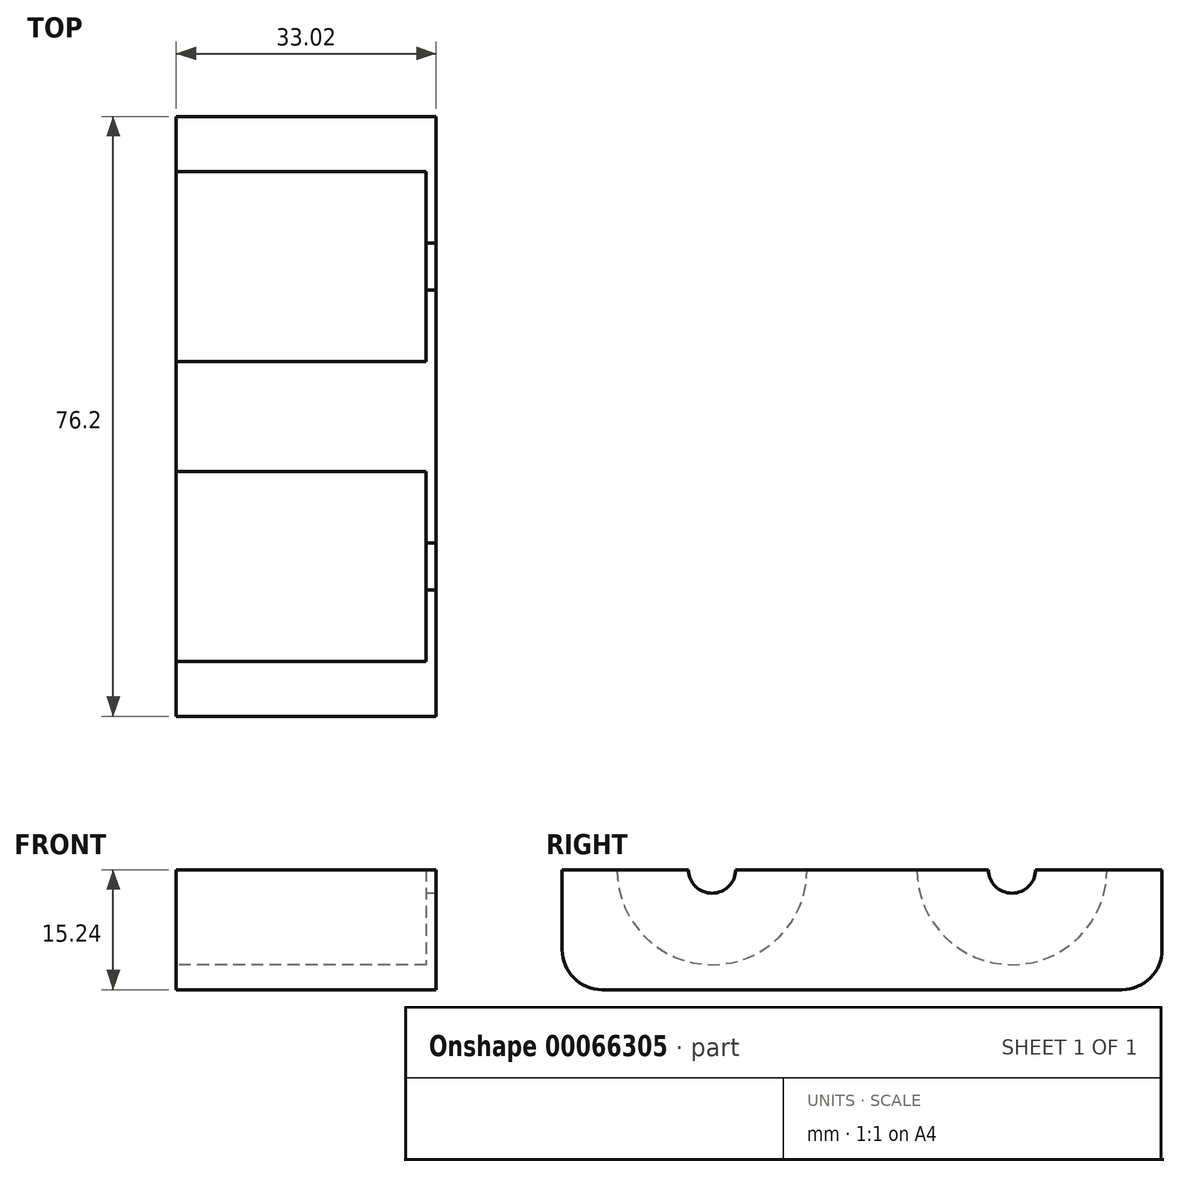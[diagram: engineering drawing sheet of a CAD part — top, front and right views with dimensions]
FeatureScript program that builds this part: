
annotation { "Feature Type Name" : "Feature", "Feature Type Description" : "" }
export const myFeature = defineFeature(function(context is Context, id is Id, definition is map)
    precondition{}
    {
        {
            var Q0;
            Q0=qCreatedBy(makeId("Right.planeOp"),FACE);
            var sketch = newSketch(context, id + "F0", { "sketchPlane" : qUnion([Q0])});
            skLineSegment(sketch, "E0.bottom", {"start": v(-38.1, 0) * mm, "end": v(38.1, 0) * mm});
            skLineSegment(sketch, "E0.top", {"start": v(-38.1, -15.24) * mm, "end": v(38.1, -15.24) * mm});
            skLineSegment(sketch, "E0.left", {"start": v(-38.1, 0) * mm, "end": v(-38.1, -15.24) * mm});
            skLineSegment(sketch, "E0.right", {"start": v(38.1, 0) * mm, "end": v(38.1, -15.24) * mm});
            skPoint(sketch, "E1", {"position": v(9.52, 0) * mm});
            skSolve(sketch);
        }
        {
            var Q0;
            Q0=makeQuery(id+"F0.imprint","IMPRINT",FACE,{"disambiguationData":[TD([[makeQuery(id+"F0.imprint","IMPRINT",EDGE,{"derivedFrom":sQuery(id+"F0.wireOp",EDGE,"E0.bottom")}),-1.0]])]});
            extrude(context, id + "F1", {"entities" : qUnion([Q0]), "depth" : 33.02 * mm});
        }
        {
            var Q0;
            Q0=qCreatedBy(makeId("Right.planeOp"),FACE);
            var sketch = newSketch(context, id + "F2", { "sketchPlane" : qUnion([Q0])});
            skPoint(sketch, "E2", {"position": v(19.05, 0) * mm});
            skCircle(sketch, "E3", {"center": v(19.05, 0) * mm, "radius": 12.07 * mm});
            skCircle(sketch, "E4.MirrorC", {"center": v(-19.05, 0) * mm, "radius": 12.07 * mm});
            skSolve(sketch);
        }
        {
            var Q0;
            Q0 = qSketchRegion(id + "F2", true);
            extrude(context, id + "F3", {"entities" : qUnion([Q0]), "operationType" : NewBodyOperationType.REMOVE, "depth" : 31.75 * mm});
        }
        {
            var Q0;
            Q0=qCreatedBy(makeId("Right.planeOp"),FACE);
            var sketch = newSketch(context, id + "F4", { "sketchPlane" : qUnion([Q0])});
            skPoint(sketch, "E5.0", {"position": v(9.52, 0) * mm});
            skArc(sketch, "E6.0", {"start": v(6.98, 0) * mm, "mid": v(19.05, -12.07) * mm, "end": v(31.11, 0) * mm});
            skCircle(sketch, "E7", {"center": v(19.05, 0) * mm, "radius": 2.98 * mm});
            skCircle(sketch, "E8.MirrorC", {"center": v(-19.05, 0) * mm, "radius": 2.98 * mm});
            skSolve(sketch);
        }
        {
            var Q0;
            Q0 = qSketchRegion(id + "F4", true);
            extrude(context, id + "F5", {"entities" : qUnion([Q0]), "operationType" : NewBodyOperationType.REMOVE, "depth" : 50.8 * mm});
        }
        {
            var Q0;
            Q0=makeQuery(id+"F1.opExtrude","SWEPT_EDGE",EDGE,{"disambiguationData":[OSD([sQuery(id+"F0.wireOp",EDGE,"E0.top"),sQuery(id+"F0.wireOp",EDGE,"E0.left")])]});
            var Q1;
            Q1=makeQuery(id+"F1.opExtrude","SWEPT_EDGE",EDGE,{"disambiguationData":[OSD([sQuery(id+"F0.wireOp",EDGE,"E0.top"),sQuery(id+"F0.wireOp",EDGE,"E0.right")])]});
            fillet(context, id + "F6", {"entities" : qUnion([Q0, Q1]), "radius" : 5.08 * mm, "tangentPropagation" : true, "allowEdgeOverflow" : false});
        }
    });
